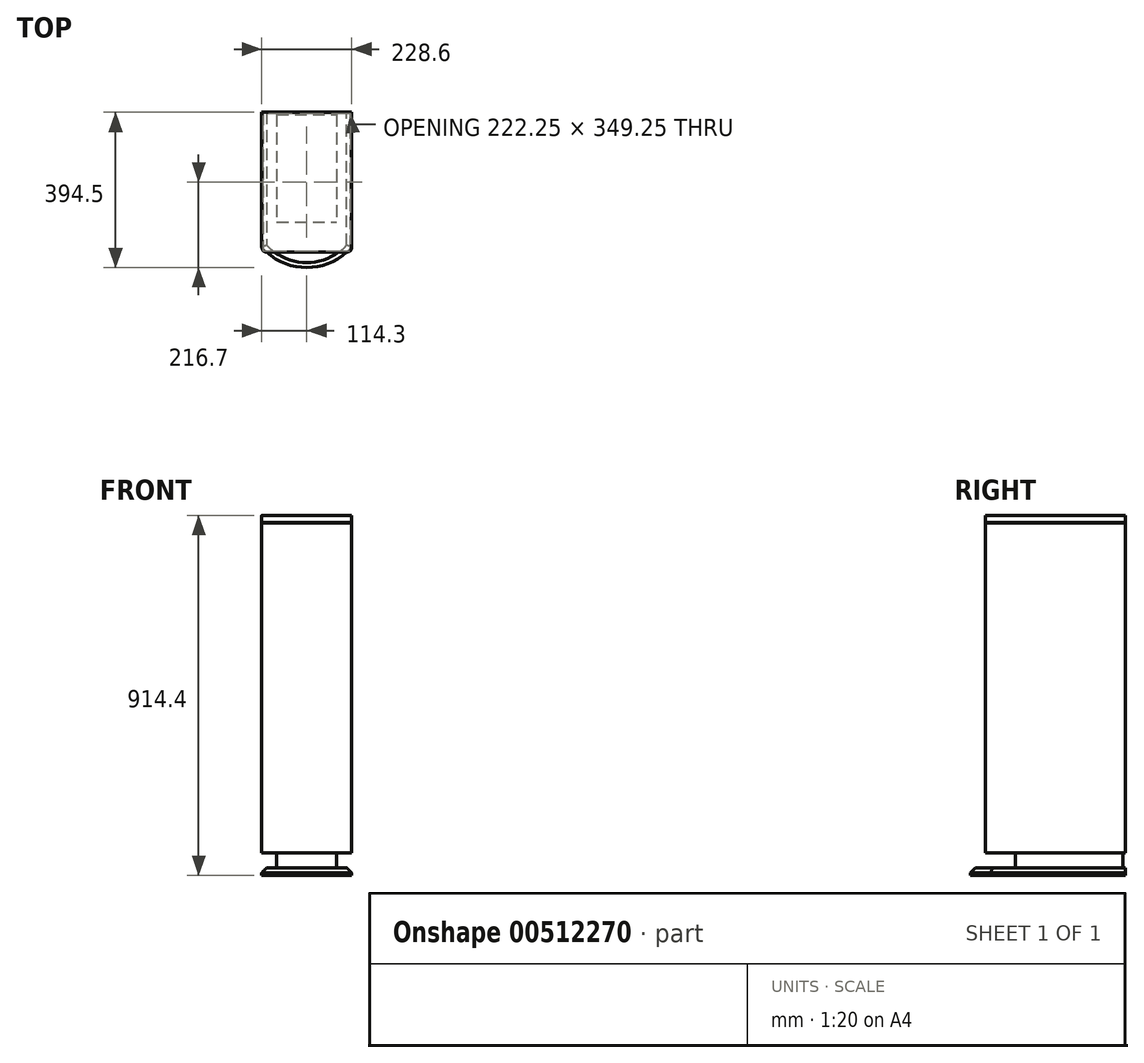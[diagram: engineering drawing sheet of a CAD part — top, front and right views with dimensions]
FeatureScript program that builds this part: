
annotation { "Feature Type Name" : "Feature", "Feature Type Description" : "" }
export const myFeature = defineFeature(function(context is Context, id is Id, definition is map)
    precondition{}
    {
        {
            var Q0;
            Q0=qCreatedBy(makeId("Top.planeOp"),FACE);
            var sketch = newSketch(context, id + "F0", { "sketchPlane" : qUnion([Q0])});
            skLineSegment(sketch, "E0", {"start": v(-114.3, -165.1) * mm, "end": v(-114.3, 177.8) * mm});
            skLineSegment(sketch, "E1", {"start": v(-114.3, 177.8) * mm, "end": v(114.3, 177.8) * mm});
            skLineSegment(sketch, "E2", {"start": v(114.3, 177.8) * mm, "end": v(114.3, -165.1) * mm});
            skLineSegment(sketch, "E3", {"start": v(101.6, -177.8) * mm, "end": v(-101.6, -177.8) * mm});
            skArc(sketch, "E4", {"start": v(-114.3, -165.1) * mm, "mid": v(-110.58, -174.08) * mm, "end": v(-101.6, -177.8) * mm});
            skArc(sketch, "E5", {"start": v(101.6, -177.8) * mm, "mid": v(110.58, -174.08) * mm, "end": v(114.3, -165.1) * mm});
            skSolve(sketch);
        }
        {
            var Q0;
            Q0=makeQuery(id+"F0.imprint","IMPRINT",FACE,{"disambiguationData":[TD([[makeQuery(id+"F0.imprint","IMPRINT",EDGE,{"derivedFrom":sQuery(id+"F0.wireOp",EDGE,"E0")}),-1.0]])]});
            extrude(context, id + "F1", {"entities" : qUnion([Q0]), "depth" : 838.2 * mm});
        }
        {
            var Q0;
            Q0=makeQuery(id+"F1.opExtrude","CAP_FACE",FACE,{"disambiguationData":[OSD([sQuery(id+"F0.wireOp",EDGE,"E0"),sQuery(id+"F0.wireOp",EDGE,"E1"),sQuery(id+"F0.wireOp",EDGE,"E2"),sQuery(id+"F0.wireOp",EDGE,"E3"),sQuery(id+"F0.wireOp",EDGE,"E4"),sQuery(id+"F0.wireOp",EDGE,"E5")])],"isStart":false});
            var sketch = newSketch(context, id + "F2", { "sketchPlane" : qUnion([Q0])});
            skArc(sketch, "E6.0", {"start": v(-111.12, -165.1) * mm, "mid": v(-108.34, -171.84) * mm, "end": v(-101.6, -174.63) * mm});
            skArc(sketch, "E6.1", {"start": v(101.6, -174.63) * mm, "mid": v(108.34, -171.84) * mm, "end": v(111.12, -165.1) * mm});
            skLineSegment(sketch, "E6.2", {"start": v(111.13, -165.1) * mm, "end": v(111.12, 174.62) * mm});
            skLineSegment(sketch, "E6.3", {"start": v(-101.6, -174.62) * mm, "end": v(101.6, -174.62) * mm});
            skLineSegment(sketch, "E6.4", {"start": v(111.12, 174.62) * mm, "end": v(-111.13, 174.62) * mm});
            skLineSegment(sketch, "E6.5", {"start": v(-111.13, 174.63) * mm, "end": v(-111.12, -165.1) * mm});
            skSolve(sketch);
        }
        {
            var Q0;
            Q0=makeQuery(id+"F2.imprint","IMPRINT",FACE,{"disambiguationData":[TD([[makeQuery(id+"F2.imprint","IMPRINT",EDGE,{"derivedFrom":sQuery(id+"F2.wireOp",EDGE,"E6.0")}),1.0]])]});
            extrude(context, id + "F3", {"entities" : qUnion([Q0]), "operationType" : NewBodyOperationType.ADD, "depth" : 1.59 * mm});
        }
        {
            var Q0;
            Q0=makeQuery(id+"F3.opExtrude","CAP_FACE",FACE,{"disambiguationData":[OSD([sQuery(id+"F2.wireOp",EDGE,"E6.0"),sQuery(id+"F2.wireOp",EDGE,"E6.1"),sQuery(id+"F2.wireOp",EDGE,"E6.2"),sQuery(id+"F2.wireOp",EDGE,"E6.3"),sQuery(id+"F2.wireOp",EDGE,"E6.4"),sQuery(id+"F2.wireOp",EDGE,"E6.5")])],"isStart":false});
            var sketch = newSketch(context, id + "F4", { "sketchPlane" : qUnion([Q0])});
            skArc(sketch, "E7.0", {"start": v(101.6, -177.8) * mm, "mid": v(110.58, -174.08) * mm, "end": v(114.3, -165.1) * mm});
            skLineSegment(sketch, "E7.1", {"start": v(114.3, 177.8) * mm, "end": v(-114.3, 177.8) * mm});
            skLineSegment(sketch, "E7.2", {"start": v(-114.3, 177.8) * mm, "end": v(-114.3, -165.1) * mm});
            skLineSegment(sketch, "E7.3", {"start": v(114.3, -165.1) * mm, "end": v(114.3, 177.8) * mm});
            skArc(sketch, "E7.4", {"start": v(-114.3, -165.1) * mm, "mid": v(-110.58, -174.08) * mm, "end": v(-101.6, -177.8) * mm});
            skLineSegment(sketch, "E7.5", {"start": v(-101.6, -177.8) * mm, "end": v(101.6, -177.8) * mm});
            skSolve(sketch);
        }
        {
            var Q0;
            Q0=qSketchRegion(id+"F4",true);
            extrude(context, id + "F5", {"entities" : qUnion([Q0]), "operationType" : NewBodyOperationType.ADD, "depth" : 17.46 * mm});
        }
        {
            var Q0;
            Q0=makeQuery(id+"F1.opExtrude","CAP_FACE",FACE,{"disambiguationData":[OSD([sQuery(id+"F0.wireOp",EDGE,"E0"),sQuery(id+"F0.wireOp",EDGE,"E1"),sQuery(id+"F0.wireOp",EDGE,"E2"),sQuery(id+"F0.wireOp",EDGE,"E3"),sQuery(id+"F0.wireOp",EDGE,"E4"),sQuery(id+"F0.wireOp",EDGE,"E5")])],"isStart":true});
            var sketch = newSketch(context, id + "F6", { "sketchPlane" : qUnion([Q0])});
            skLineSegment(sketch, "E8.bottom", {"start": v(-76.2, -171.45) * mm, "end": v(76.2, -171.45) * mm});
            skLineSegment(sketch, "E8.top", {"start": v(-76.2, 101.6) * mm, "end": v(76.2, 101.6) * mm});
            skLineSegment(sketch, "E8.left", {"start": v(-76.2, -171.45) * mm, "end": v(-76.2, 101.6) * mm});
            skLineSegment(sketch, "E8.right", {"start": v(76.2, -171.45) * mm, "end": v(76.2, 101.6) * mm});
            skSolve(sketch);
        }
        {
            var Q0;
            Q0=makeQuery(id+"F6.imprint","IMPRINT",FACE,{"disambiguationData":[TD([[makeQuery(id+"F6.imprint","IMPRINT",EDGE,{"derivedFrom":sQuery(id+"F6.wireOp",EDGE,"E8.bottom")}),1.0]])]});
            extrude(context, id + "F7", {"entities" : qUnion([Q0]), "operationType" : NewBodyOperationType.ADD, "depth" : 38.1 * mm});
        }
        {
            var Q0;
            Q0=makeQuery(id+"F7.opExtrude","CAP_FACE",FACE,{"disambiguationData":[OSD([sQuery(id+"F6.wireOp",EDGE,"E8.bottom"),sQuery(id+"F6.wireOp",EDGE,"E8.top"),sQuery(id+"F6.wireOp",EDGE,"E8.left"),sQuery(id+"F6.wireOp",EDGE,"E8.right")])],"isStart":false});
            var sketch = newSketch(context, id + "F8", { "sketchPlane" : qUnion([Q0])});
            skLineSegment(sketch, "E9.bottom", {"start": v(-114.3, -177.8) * mm, "end": v(114.3, -177.8) * mm});
            skLineSegment(sketch, "E9.left", {"start": v(-114.3, -177.8) * mm, "end": v(-114.3, 165.1) * mm});
            skLineSegment(sketch, "E9.right", {"start": v(114.3, -177.8) * mm, "end": v(114.3, 165.1) * mm});
            skArc(sketch, "E10", {"start": v(114.3, 165.1) * mm, "mid": v(0, 216.7) * mm, "end": v(-114.3, 165.1) * mm});
            skSolve(sketch);
        }
        {
            var Q0;
            Q0=makeQuery(id+"F8.imprint","IMPRINT",FACE,{"disambiguationData":[TD([[makeQuery(id+"F8.imprint","IMPRINT",EDGE,{"derivedFrom":sQuery(id+"F8.wireOp",EDGE,"E9.bottom")}),1.0]])]});
            var Q1;
            Q1=makeQuery(id+"F8.imprint","IMPRINT",FACE,{"disambiguationData":[TD([[makeQuery(id+"F8.imprint","IMPRINT",EDGE,{"derivedFrom":makeQuery(id+"F7.opExtrude","CAP_EDGE",EDGE,{"disambiguationData":[OSD([sQuery(id+"F6.wireOp",EDGE,"E8.bottom")])],"isStart":false})}),1.0]])]});
            extrude(context, id + "F9", {"entities" : qUnion([Q0, Q1]), "depth" : 19.05 * mm});
        }
        {
            var Q0;
            Q0=makeQuery(id+"F9.opExtrude","CAP_EDGE",EDGE,{"disambiguationData":[OSD([sQuery(id+"F8.wireOp",EDGE,"E9.left")])],"isStart":true});
            var Q1;
            Q1=makeQuery(id+"F9.opExtrude","CAP_EDGE",EDGE,{"disambiguationData":[OSD([sQuery(id+"F8.wireOp",EDGE,"E10")])],"isStart":true});
            var Q2;
            Q2=makeQuery(id+"F9.opExtrude","CAP_EDGE",EDGE,{"disambiguationData":[OSD([sQuery(id+"F8.wireOp",EDGE,"E9.right")])],"isStart":true});
            chamfer(context, id + "F10", {"entities" : qUnion([Q0, Q1, Q2]), "width" : 12.7 * mm, "tangentPropagation" : true});
        }
    });
